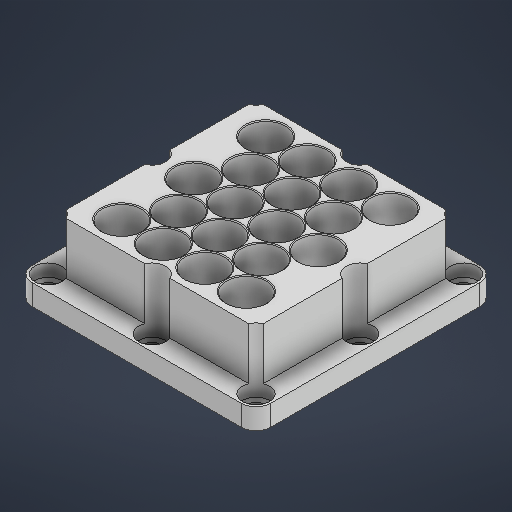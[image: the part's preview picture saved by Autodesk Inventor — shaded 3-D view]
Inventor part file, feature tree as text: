
AUTODESK INVENTOR PART (.ipt)
format: ipt  version: 2025 (Build 290162000, 162)  size: 387,584 bytes
history: native  units: in
note: dims shown in document units (in); Inventor stores cm internally (conversion verified against a paired STEP export)
features: sketch x6, extrude x2, hole x1, fillet x1, chamfer x1
ambient origin geometry x8: Origin, YZ Plane, XZ Plane, XY Plane, X Axis, Y Axis, Z Axis, Center Point
bodies: Solid1 (feature_tree)
feature tree (11):
  extrude  "Extrusion1"  Depth=4.5276in
  extrude  "Extrusion2"  Depth=3.7402in
  hole  "Hole3"  [1 undecoded]
  fillet  "Fillet1"  Radius=1.3638in
  chamfer  "Chamfer1"  Distance=0.7874in
  sketch  "Sketch1"  dims[d0=4.5276in d1=4.5276in]
  sketch  "Sketch4"  dims[d2=0.3937in d3=0.0in d48=3.7402in]
  sketch  "Sketch Rectangular Pattern11"  dims[d132=2.3622in]
  sketch  "Sketch Rectangular Pattern12"  dims[d133=2.7276in]
  sketch  "Sketch5"  dims[d49=3.7402in d57=0.9843in d58=0.0in d124=1.3638in]
  sketch  "Sketch Rectangular Pattern13"  dims[d134=0.748in d135=1.5748in d137=0.7874in d138=1.1811in d140=1.3638in d143=0.748in d146=0.3937in d147=0.6819in d148=1.1811in d150=0.7874in d151=0.7874in d153=1.3638in d156=3.937in d157=3.937in d158=0.2756in d159=1.1811in d161=1.9685in d162=1.1811in d164=1.9685in d167=0.2805in d168=0.2362in d169=0.5118in d170=1.2205in d171=90.0deg d172=0.315in d173=0.8108in d174=0.2805in d175=0.0157in d176=0.0787in d177=45.0deg]
note: 1 required parameter value undecoded (feature->parameter linkage not recoverable at this tier; creation-order binding heuristic only, values carry confidence <= 0.55)
